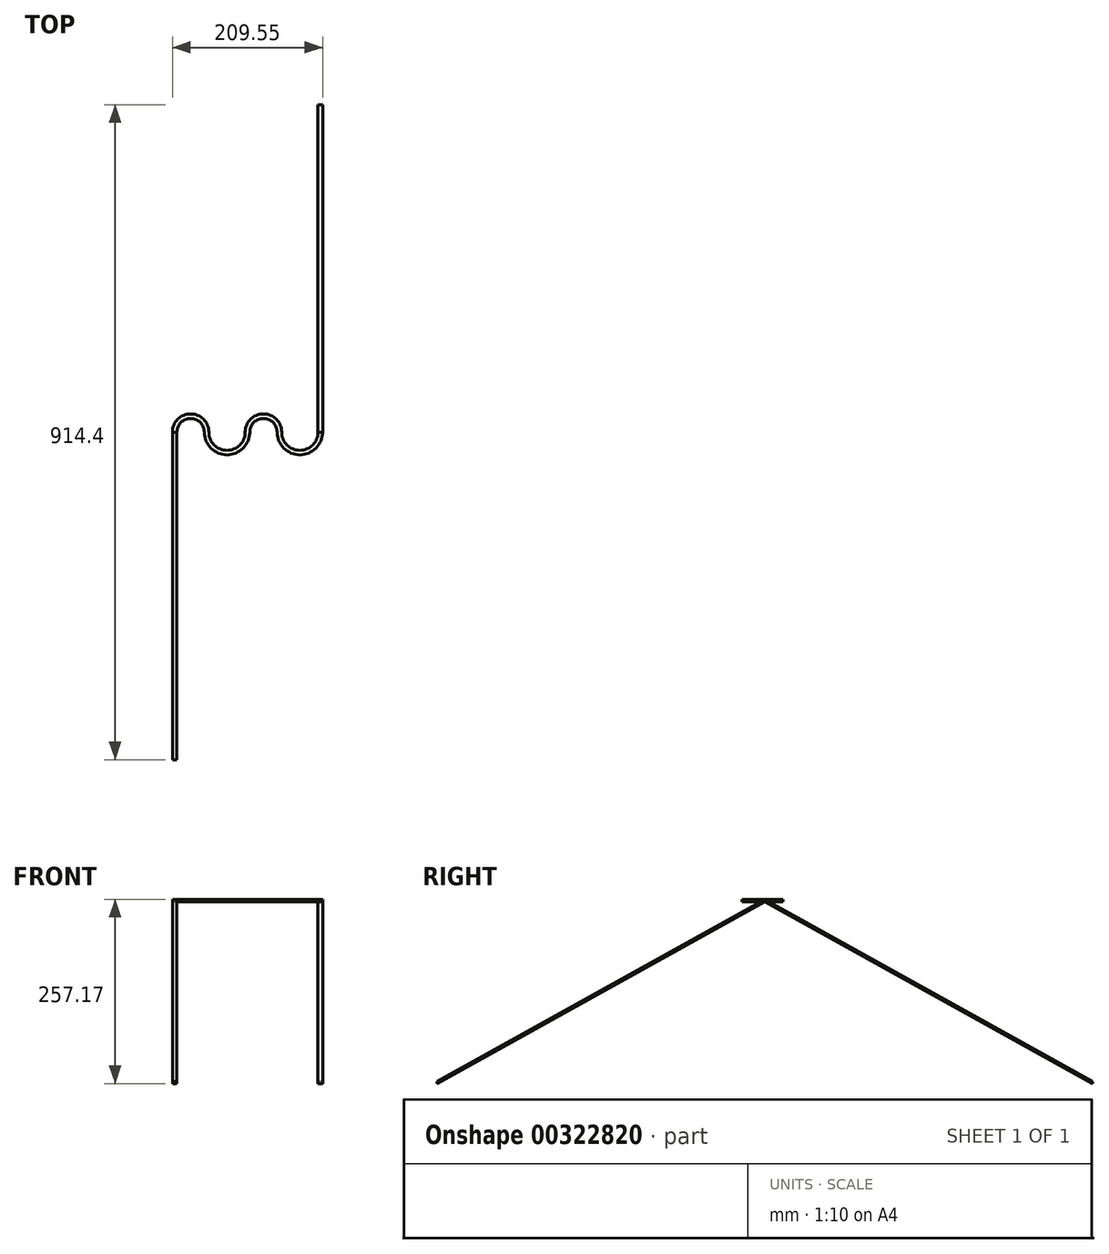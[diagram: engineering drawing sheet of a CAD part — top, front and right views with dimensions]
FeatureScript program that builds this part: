
annotation { "Feature Type Name" : "Feature", "Feature Type Description" : "" }
export const myFeature = defineFeature(function(context is Context, id is Id, definition is map)
    precondition{}
    {
        {
            var Q0;
            Q0=qCreatedBy(makeId("Top.planeOp"),FACE);
            var sketch = newSketch(context, id + "F0", { "sketchPlane" : qUnion([Q0])});
            skArc(sketch, "E0", {"start": v(-50.8, 0) * mm, "mid": v(-76.2, 25.4) * mm, "end": v(-101.6, 0) * mm});
            skArc(sketch, "E1", {"start": v(-50.8, 0) * mm, "mid": v(-25.4, -25.4) * mm, "end": v(0, 0) * mm});
            skArc(sketch, "E2", {"start": v(50.8, 0) * mm, "mid": v(25.4, 25.4) * mm, "end": v(0, 0) * mm});
            skArc(sketch, "E3", {"start": v(50.8, 0) * mm, "mid": v(76.2, -25.4) * mm, "end": v(101.6, 0) * mm});
            skArc(sketch, "E4.0", {"start": v(44.45, 0) * mm, "mid": v(76.2, -31.75) * mm, "end": v(107.95, 0) * mm});
            skArc(sketch, "E4.1", {"start": v(44.45, 0) * mm, "mid": v(25.4, 19.05) * mm, "end": v(6.35, 0) * mm});
            skArc(sketch, "E4.2", {"start": v(-57.15, 0) * mm, "mid": v(-25.4, -31.75) * mm, "end": v(6.35, 0) * mm});
            skArc(sketch, "E4.3", {"start": v(-57.15, 0) * mm, "mid": v(-76.2, 19.05) * mm, "end": v(-95.25, 0) * mm});
            skLineSegment(sketch, "E5", {"start": v(-101.6, 0) * mm, "end": v(-95.25, 0) * mm});
            skLineSegment(sketch, "E6", {"start": v(101.6, 0) * mm, "end": v(107.95, 0) * mm});
            skSolve(sketch);
        }
        {
            var Q0;
            Q0=qCreatedBy(makeId("Right.planeOp"),FACE);
            var sketch = newSketch(context, id + "F1", { "sketchPlane" : qUnion([Q0])});
            skLineSegment(sketch, "E7", {"start": v(0, 0) * mm, "end": v(-457.2, -254) * mm});
            skLineSegment(sketch, "E8", {"start": v(0, 3.17) * mm, "end": v(-457.2, -250.83) * mm});
            skLineSegment(sketch, "E9", {"start": v(0, 3.17) * mm, "end": v(0, 0) * mm});
            skLineSegment(sketch, "E10", {"start": v(-457.2, -250.83) * mm, "end": v(-457.2, -254) * mm});
            skSolve(sketch);
        }
        {
            var Q0;
            Q0 = qSketchRegion(id + "F1", true);
            extrude(context, id + "F2", {"entities" : qUnion([Q0]), "oppositeDirection" : true, "depth" : 101.6 * mm});
        }
        {
            var Q0;
            Q0 = qSketchRegion(id + "F1", true);
            extrude(context, id + "F3", {"entities" : qUnion([Q0]), "operationType" : NewBodyOperationType.REMOVE, "oppositeDirection" : true, "depth" : 95.25 * mm});
        }
        {
            var Q0;
            Q0=qCreatedBy(makeId("Right.planeOp"),FACE);
            var sketch = newSketch(context, id + "F4", { "sketchPlane" : qUnion([Q0])});
            skLineSegment(sketch, "E11", {"start": v(0, 0) * mm, "end": v(457.2, -254) * mm});
            skLineSegment(sketch, "E12", {"start": v(0, 3.17) * mm, "end": v(457.2, -250.83) * mm});
            skLineSegment(sketch, "E13", {"start": v(0, 3.17) * mm, "end": v(0, 0) * mm});
            skLineSegment(sketch, "E14", {"start": v(457.2, -250.82) * mm, "end": v(457.2, -254) * mm});
            skSolve(sketch);
        }
        {
            var Q0;
            Q0 = qSketchRegion(id + "F4", true);
            extrude(context, id + "F5", {"entities" : qUnion([Q0]), "operationType" : NewBodyOperationType.ADD, "depth" : 107.95 * mm});
        }
        {
            var Q0;
            Q0 = qSketchRegion(id + "F4", true);
            extrude(context, id + "F6", {"entities" : qUnion([Q0]), "operationType" : NewBodyOperationType.REMOVE, "depth" : 101.6 * mm});
        }
        {
            var Q0;
            Q0 = qSketchRegion(id + "F0", true);
            extrude(context, id + "F7", {"entities" : qUnion([Q0]), "operationType" : NewBodyOperationType.ADD, "depth" : 3.17 * mm});
        }
    });
